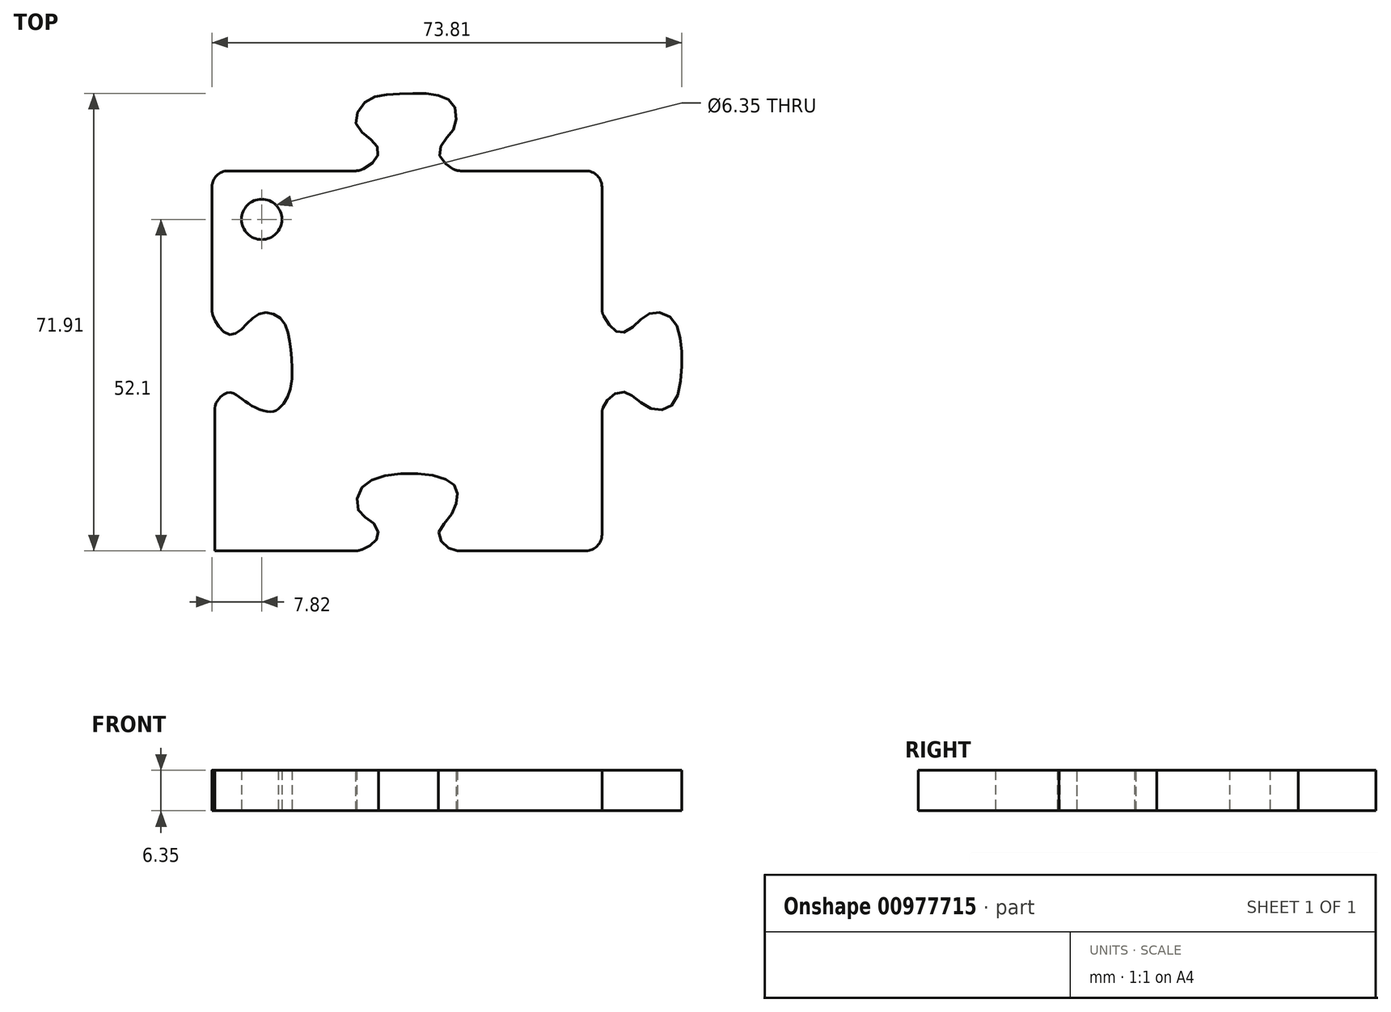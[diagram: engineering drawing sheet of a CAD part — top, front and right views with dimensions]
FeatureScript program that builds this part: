
annotation { "Feature Type Name" : "Feature", "Feature Type Description" : "" }
export const myFeature = defineFeature(function(context is Context, id is Id, definition is map)
    precondition{}
    {
        {
            var Q0;
            Q0=qCreatedBy(makeId("Top.planeOp"),FACE);
            var sketch = newSketch(context, id + "F0", { "sketchPlane" : qUnion([Q0])});
            skLineSegment(sketch, "E0.bottom", {"start": v(38.1, 38.1) * mm, "end": v(-38.1, 38.1) * mm, "construction": true});
            skLineSegment(sketch, "E0.top", {"start": v(38.1, -38.1) * mm, "end": v(-38.1, -38.1) * mm, "construction": true});
            skLineSegment(sketch, "E0.left", {"start": v(38.1, 38.1) * mm, "end": v(38.1, -38.1) * mm, "construction": true});
            skLineSegment(sketch, "E0.right", {"start": v(-38.1, 38.1) * mm, "end": v(-38.1, -38.1) * mm, "construction": true});
            skPoint(sketch, "E0.middle", {"position": v(0, 0) * mm});
            skLineSegment(sketch, "E1", {"start": v(-34.74, 25.07) * mm, "end": v(-14.72, 25.07) * mm});
            skLineSegment(sketch, "E2", {"start": v(1.8, 25.07) * mm, "end": v(21.44, 25.07) * mm});
            skLineSegment(sketch, "E3", {"start": v(23.98, 22.53) * mm, "end": v(23.98, 3.43) * mm});
            skLineSegment(sketch, "E4", {"start": v(23.98, -13.05) * mm, "end": v(23.98, -32.1) * mm});
            skLineSegment(sketch, "E5", {"start": v(21.44, -34.65) * mm, "end": v(1.58, -34.65) * mm});
            skLineSegment(sketch, "E6", {"start": v(-14.73, -34.65) * mm, "end": v(-36.83, -34.65) * mm});
            skLineSegment(sketch, "E7", {"start": v(-36.83, -34.65) * mm, "end": v(-36.83, -12.61) * mm});
            skLineSegment(sketch, "E8", {"start": v(-37.28, 22.53) * mm, "end": v(-37.28, 3.23) * mm});
            skFitSpline(sketch, "E9", {"points": [v(-37.28, 2.8) * mm, v(-36.64, 1.29) * mm, v(-35.04, -0.48) * mm, v(-33.35, -0.4) * mm, v(-31.2, 1.66) * mm, v(-28.94, 2.8) * mm, v(-26.31, 1.7) * mm, v(-25.12, -1.43) * mm, v(-24.7, -5.26) * mm, v(-25.16, -9.99) * mm, v(-26.89, -12.38) * mm], "startDerivative": vector(6.42, -18.91) * mm, "endDerivative": vector(-20.24, -18.94) * mm});
            skFitSpline(sketch, "E10", {"points": [v(-26.89, -12.38) * mm, v(-28.16, -12.79) * mm, v(-30.88, -11.92) * mm, v(-33.06, -10.4) * mm, v(-34.79, -9.78) * mm, v(-36.64, -11.43) * mm, v(-36.83, -12.61) * mm], "startDerivative": vector(-7.22, -6.07) * mm, "endDerivative": vector(0.38, -8.5) * mm});
            skFitSpline(sketch, "E11", {"points": [v(-14.1, 25.07) * mm, v(-11.66, 26.72) * mm, v(-11.17, 28.59) * mm, v(-12.9, 30.5) * mm, v(-14.68, 32.77) * mm, v(-13.17, 35.92) * mm, v(-9.97, 37.03) * mm, v(-5.62, 37.26) * mm, v(-1.48, 36.9) * mm, v(0.74, 35.39) * mm, v(0.87, 32.06) * mm, v(-0.64, 29.97) * mm, v(-1.57, 27.66) * mm, v(0, 25.74) * mm, v(1.21, 25.07) * mm], "startDerivative": vector(38.72, 19.86) * mm, "endDerivative": vector(22.38, -10.51) * mm});
            skArc(sketch, "E12.filletArc", {"start": v(-14.72, 25.07) * mm, "mid": v(-14.1, 25.15) * mm, "end": v(-13.53, 25.37) * mm});
            skArc(sketch, "E13.filletArc", {"start": v(0.58, 25.38) * mm, "mid": v(1.17, 25.15) * mm, "end": v(1.8, 25.07) * mm});
            skArc(sketch, "E14.filletArc", {"start": v(-37.28, 3.23) * mm, "mid": v(-37.24, 2.8) * mm, "end": v(-37.12, 2.36) * mm});
            skPoint(sketch, "E15.visualSharp", {"position": v(-37.28, 25.07) * mm});
            skArc(sketch, "E15.filletArc", {"start": v(-34.74, 25.07) * mm, "mid": v(-36.53, 24.33) * mm, "end": v(-37.28, 22.53) * mm});
            skPoint(sketch, "E16.visualSharp", {"position": v(23.98, 25.07) * mm});
            skArc(sketch, "E16.filletArc", {"start": v(23.98, 22.53) * mm, "mid": v(23.23, 24.33) * mm, "end": v(21.44, 25.07) * mm});
            skFitSpline(sketch, "E17", {"points": [v(23.98, 2.8) * mm, v(25.52, 0.39) * mm, v(27.2, -0.36) * mm, v(29.53, 1.22) * mm, v(31.86, 2.8) * mm, v(34.85, 1.93) * mm, v(36.35, -1.55) * mm, v(36.4, -7.14) * mm, v(35.03, -11.72) * mm, v(32.12, -12.42) * mm, v(29.09, -10.58) * mm, v(27.2, -9.65) * mm, v(24.9, -10.84) * mm, v(23.98, -12.6) * mm], "startDerivative": vector(18.91, -35.94) * mm, "endDerivative": vector(-10.25, -29.43) * mm});
            skArc(sketch, "E18.filletArc", {"start": v(23.98, 3.43) * mm, "mid": v(24.05, 2.8) * mm, "end": v(24.28, 2.22) * mm});
            skArc(sketch, "E19.filletArc", {"start": v(24.14, -12.14) * mm, "mid": v(24.02, -12.59) * mm, "end": v(23.98, -13.05) * mm});
            skPoint(sketch, "E20.visualSharp", {"position": v(23.98, -34.65) * mm});
            skArc(sketch, "E20.filletArc", {"start": v(21.44, -34.65) * mm, "mid": v(23.23, -33.9) * mm, "end": v(23.98, -32.1) * mm});
            skFitSpline(sketch, "E21", {"points": [v(-14.2, -34.65) * mm, v(-12.28, -33.67) * mm, v(-11.13, -32.16) * mm, v(-12.02, -30.22) * mm, v(-14.2, -28.43) * mm, v(-13.9, -24.94) * mm, v(-9.94, -22.83) * mm, v(-3.05, -22.72) * mm, v(0.61, -24.19) * mm, v(1.26, -26.2) * mm, v(0, -29.43) * mm, v(-1.68, -31.98) * mm, v(-0.32, -34.06) * mm, v(1.35, -34.65) * mm], "startDerivative": vector(30.63, 12.93) * mm, "endDerivative": vector(27.87, -5.12) * mm});
            skArc(sketch, "E22.filletArc", {"start": v(1.1, -34.6) * mm, "mid": v(1.34, -34.64) * mm, "end": v(1.58, -34.65) * mm});
            skArc(sketch, "E23.filletArc", {"start": v(-14.73, -34.65) * mm, "mid": v(-14.2, -34.6) * mm, "end": v(-13.7, -34.43) * mm});
            skLineSegment(sketch, "E24", {"start": v(-37.28, 25.07) * mm, "end": v(23.98, -34.65) * mm, "construction": true});
            skCircle(sketch, "E25", {"center": v(-29.46, 17.45) * mm, "radius": 3.18 * mm});
            skSolve(sketch);
        }
        {
            var Q0;
            Q0=qSketchRegion(id+"F0",true);
            extrude(context, id + "F1", {"entities" : qUnion([Q0]), "depth" : 6.35 * mm});
        }
    });
